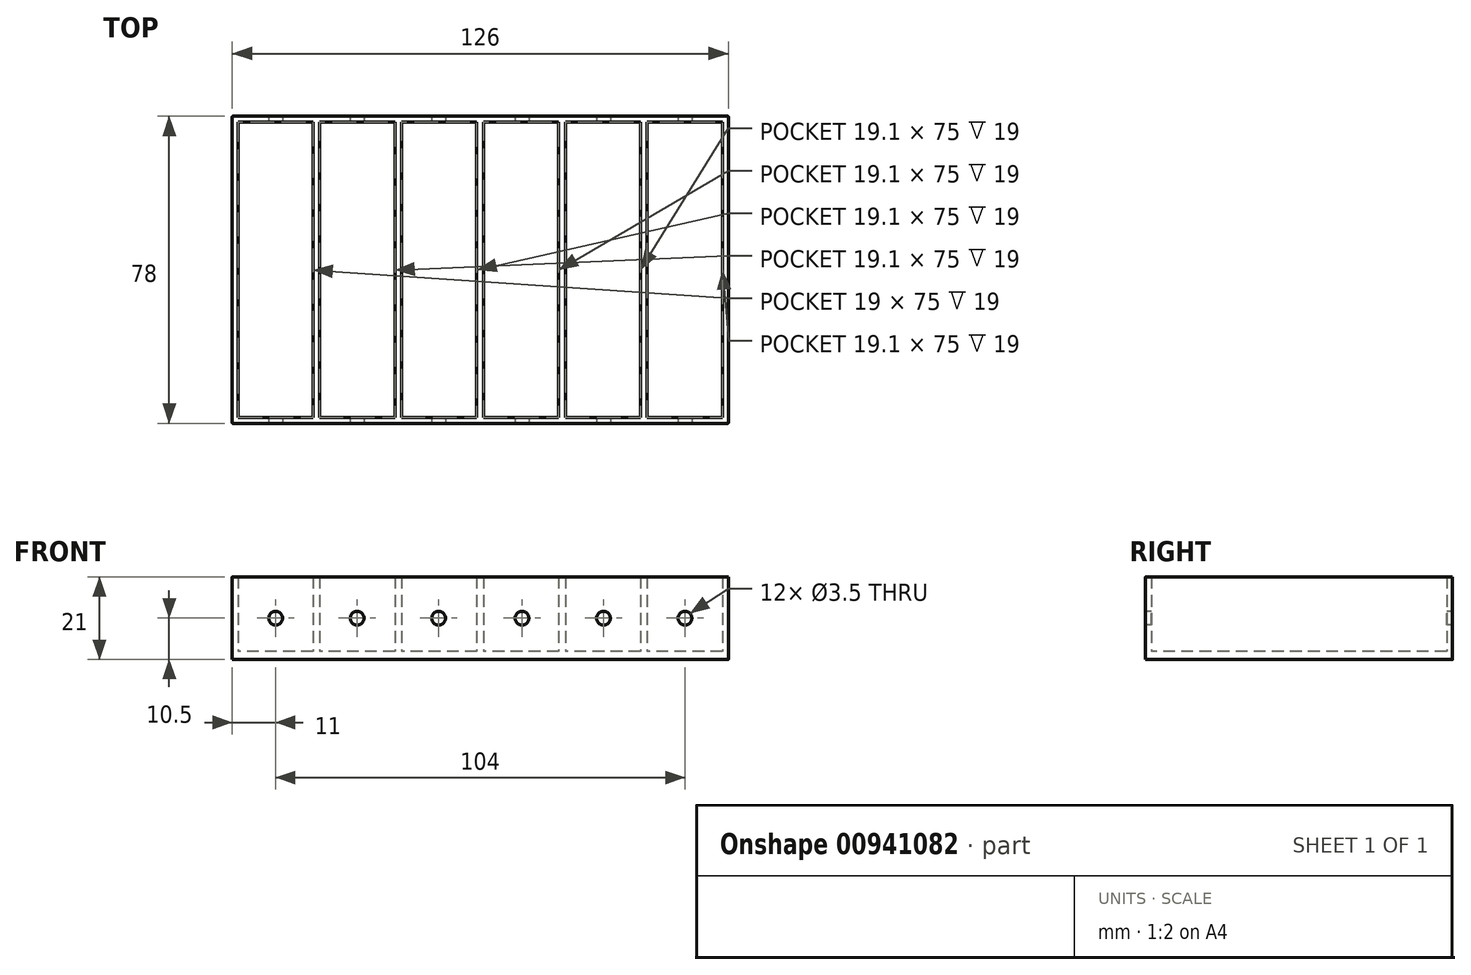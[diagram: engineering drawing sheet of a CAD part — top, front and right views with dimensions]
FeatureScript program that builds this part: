
annotation { "Feature Type Name" : "Feature", "Feature Type Description" : "" }
export const myFeature = defineFeature(function(context is Context, id is Id, definition is map)
    precondition{}
    {
        {
            var Q0;
            Q0=qCreatedBy(makeId("Top.planeOp"),FACE);
            var sketch = newSketch(context, id + "F0", { "sketchPlane" : qUnion([Q0]), "disableImprinting" : false});
            skLineSegment(sketch, "E0.bottom", {"start": v(63, 39) * mm, "end": v(-63, 39) * mm});
            skLineSegment(sketch, "E0.top", {"start": v(63, -39) * mm, "end": v(-63, -39) * mm});
            skLineSegment(sketch, "E0.left", {"start": v(63, 39) * mm, "end": v(63, -39) * mm});
            skLineSegment(sketch, "E0.right", {"start": v(-63, 39) * mm, "end": v(-63, -39) * mm});
            skPoint(sketch, "E0.middle", {"position": v(0, 0) * mm});
            skSolve(sketch);
        }
        {
            var Q0;
            Q0 = qSketchRegion(id + "F0", true);
            extrude(context, id + "F1", {"entities" : qUnion([Q0]), "depth" : 2 * mm, "offsetDistance" : 25 * mm});
        }
        {
            var Q0;
            Q0=makeQuery(id+"F1.opExtrude","CAP_FACE",FACE,{"disambiguationData":[OSD([sQuery(id+"F0.wireOp",EDGE,"E0.bottom"),sQuery(id+"F0.wireOp",EDGE,"E0.top"),sQuery(id+"F0.wireOp",EDGE,"E0.left"),sQuery(id+"F0.wireOp",EDGE,"E0.right")])],"isStart":false});
            var sketch = newSketch(context, id + "F2", { "sketchPlane" : qUnion([Q0])});
            skLineSegment(sketch, "E1.0", {"start": v(61.5, 37.5) * mm, "end": v(-61.5, 37.5) * mm});
            skLineSegment(sketch, "E1.1", {"start": v(61.5, 37.5) * mm, "end": v(61.5, -37.5) * mm});
            skLineSegment(sketch, "E1.2", {"start": v(61.5, -37.5) * mm, "end": v(-61.5, -37.5) * mm});
            skLineSegment(sketch, "E1.3", {"start": v(-61.5, 37.5) * mm, "end": v(-61.5, -37.5) * mm});
            skLineSegment(sketch, "E2.0", {"start": v(63, 39) * mm, "end": v(-63, 39) * mm});
            skLineSegment(sketch, "E2.1", {"start": v(63, 39) * mm, "end": v(63, -39) * mm});
            skLineSegment(sketch, "E2.2", {"start": v(63, -39) * mm, "end": v(-63, -39) * mm});
            skLineSegment(sketch, "E2.3", {"start": v(-63, 39) * mm, "end": v(-63, -39) * mm});
            skLineSegment(sketch, "E3.0", {"start": v(-42.5, 37.5) * mm, "end": v(-42.5, -37.5) * mm});
            skLineSegment(sketch, "E4.0", {"start": v(-40.8, 37.5) * mm, "end": v(-40.8, -37.5) * mm});
            skLineSegment(sketch, "E5.0", {"start": v(42.4, 37.5) * mm, "end": v(42.4, -37.5) * mm});
            skLineSegment(sketch, "E6.0", {"start": v(40.7, 37.5) * mm, "end": v(40.7, -37.5) * mm});
            skLineSegment(sketch, "E7.0", {"start": v(21.6, 37.5) * mm, "end": v(21.6, -37.5) * mm});
            skLineSegment(sketch, "E8.0", {"start": v(19.9, 37.5) * mm, "end": v(19.9, -37.5) * mm});
            skLineSegment(sketch, "E9.0", {"start": v(0.8, 37.5) * mm, "end": v(0.8, -37.5) * mm});
            skLineSegment(sketch, "E10.0", {"start": v(-0.9, 37.5) * mm, "end": v(-0.9, -37.5) * mm});
            skLineSegment(sketch, "E11.0", {"start": v(-20, 37.5) * mm, "end": v(-20, -37.5) * mm});
            skLineSegment(sketch, "E12.0", {"start": v(-21.7, 37.5) * mm, "end": v(-21.7, -37.5) * mm});
            skSolve(sketch);
        }
        {
            var Q0;
            Q0 = qSketchRegion(id + "F2", true);
            var Q1;
            {var subQ0=sQuery(id+"F2.wireOp",EDGE,"E3.0");Q1=makeQuery(id+"F2.imprint","IMPRINT",FACE,{"disambiguationData":[TD([[makeQuery(id+"F2.imprint","IMPRINT",EDGE,{"derivedFrom":subQ0}),1.0]])]});}
            var Q2;
            {var subQ0=sQuery(id+"F2.wireOp",EDGE,"E11.0");Q2=makeQuery(id+"F2.imprint","IMPRINT",FACE,{"disambiguationData":[TD([[makeQuery(id+"F2.imprint","IMPRINT",EDGE,{"derivedFrom":subQ0}),-1.0]])]});}
            var Q3;
            {var subQ0=sQuery(id+"F2.wireOp",EDGE,"E9.0");Q3=makeQuery(id+"F2.imprint","IMPRINT",FACE,{"disambiguationData":[TD([[makeQuery(id+"F2.imprint","IMPRINT",EDGE,{"derivedFrom":subQ0}),-1.0]])]});}
            var Q4;
            {var subQ0=sQuery(id+"F2.wireOp",EDGE,"E7.0");Q4=makeQuery(id+"F2.imprint","IMPRINT",FACE,{"disambiguationData":[TD([[makeQuery(id+"F2.imprint","IMPRINT",EDGE,{"derivedFrom":subQ0}),-1.0]])]});}
            var Q5;
            {var subQ0=sQuery(id+"F2.wireOp",EDGE,"E5.0");Q5=makeQuery(id+"F2.imprint","IMPRINT",FACE,{"disambiguationData":[TD([[makeQuery(id+"F2.imprint","IMPRINT",EDGE,{"derivedFrom":subQ0}),-1.0]])]});}
            extrude(context, id + "F3", {"entities" : qUnion([Q0, Q1, Q2, Q3, Q4, Q5]), "operationType" : NewBodyOperationType.ADD, "depth" : 19 * mm, "offsetDistance" : 25 * mm});
        }
        {
            var Q0;
            Q0=makeQuery(id+"F3.boolean.opBoolean","MERGE",FACE,{"derivedFrom":[makeQuery(id+"F1.opExtrude","SWEPT_FACE",FACE,{"disambiguationData":[OSD([sQuery(id+"F0.wireOp",EDGE,"E0.top")])]}),makeQuery(id+"F3.opExtrude","SWEPT_FACE",FACE,{"disambiguationData":[OSD([sQuery(id+"F2.wireOp",EDGE,"E2.2")])]})]});
            var sketch = newSketch(context, id + "F4", { "sketchPlane" : qUnion([Q0])});
            skLineSegment(sketch, "E13", {"start": v(-63, 10.5) * mm, "end": v(63, 10.5) * mm});
            skCircle(sketch, "E14", {"center": v(-52, 10.5) * mm, "radius": 1.75 * mm});
            skCircle(sketch, "E15", {"center": v(-31.3, 10.5) * mm, "radius": 1.75 * mm});
            skCircle(sketch, "E16", {"center": v(-10.6, 10.5) * mm, "radius": 1.75 * mm});
            skCircle(sketch, "E17.MirrorC", {"center": v(10.6, 10.5) * mm, "radius": 1.75 * mm});
            skCircle(sketch, "E18.MirrorC", {"center": v(31.3, 10.5) * mm, "radius": 1.75 * mm});
            skCircle(sketch, "E19.MirrorC", {"center": v(52, 10.5) * mm, "radius": 1.75 * mm});
            skSolve(sketch);
        }
        {
            var Q0;
            Q0 = qSketchRegion(id + "F4", true);
            extrude(context, id + "F5", {"entities" : qUnion([Q0]), "operationType" : NewBodyOperationType.REMOVE, "oppositeDirection" : true, "depth" : 100 * mm, "offsetDistance" : 25 * mm});
        }
        {
            var Q0;
            Q0=makeQuery(id+"F3.boolean.opBoolean","MERGE",EDGE,{"derivedFrom":[makeQuery(id+"F1.opExtrude","SWEPT_EDGE",EDGE,{"disambiguationData":[OSD([sQuery(id+"F0.wireOp",EDGE,"E0.top"),sQuery(id+"F0.wireOp",EDGE,"E0.right")])]}),makeQuery(id+"F3.opExtrude","SWEPT_EDGE",EDGE,{"disambiguationData":[OSD([sQuery(id+"F2.wireOp",EDGE,"E2.2"),sQuery(id+"F2.wireOp",EDGE,"E2.3")])]})]});
            var Q1;
            Q1=makeQuery(id+"F3.boolean.opBoolean","MERGE",EDGE,{"derivedFrom":[makeQuery(id+"F1.opExtrude","SWEPT_EDGE",EDGE,{"disambiguationData":[OSD([sQuery(id+"F0.wireOp",EDGE,"E0.top"),sQuery(id+"F0.wireOp",EDGE,"E0.left")])]}),makeQuery(id+"F3.opExtrude","SWEPT_EDGE",EDGE,{"disambiguationData":[OSD([sQuery(id+"F2.wireOp",EDGE,"E2.1"),sQuery(id+"F2.wireOp",EDGE,"E2.2")])]})]});
            var Q2;
            Q2=makeQuery(id+"F3.boolean.opBoolean","MERGE",EDGE,{"derivedFrom":[makeQuery(id+"F1.opExtrude","SWEPT_EDGE",EDGE,{"disambiguationData":[OSD([sQuery(id+"F0.wireOp",EDGE,"E0.bottom"),sQuery(id+"F0.wireOp",EDGE,"E0.left")])]}),makeQuery(id+"F3.opExtrude","SWEPT_EDGE",EDGE,{"disambiguationData":[OSD([sQuery(id+"F2.wireOp",EDGE,"E2.0"),sQuery(id+"F2.wireOp",EDGE,"E2.1")])]})]});
            var Q3;
            Q3=makeQuery(id+"F3.boolean.opBoolean","MERGE",EDGE,{"derivedFrom":[makeQuery(id+"F1.opExtrude","SWEPT_EDGE",EDGE,{"disambiguationData":[OSD([sQuery(id+"F0.wireOp",EDGE,"E0.bottom"),sQuery(id+"F0.wireOp",EDGE,"E0.right")])]}),makeQuery(id+"F3.opExtrude","SWEPT_EDGE",EDGE,{"disambiguationData":[OSD([sQuery(id+"F2.wireOp",EDGE,"E2.0"),sQuery(id+"F2.wireOp",EDGE,"E2.3")])]})]});
            fillet(context, id + "F6", {"entities" : qUnion([Q0, Q1, Q2, Q3]), "radius" : .1 * mm, "tangentPropagation" : true, "allowEdgeOverflow" : false});
        }
    });
